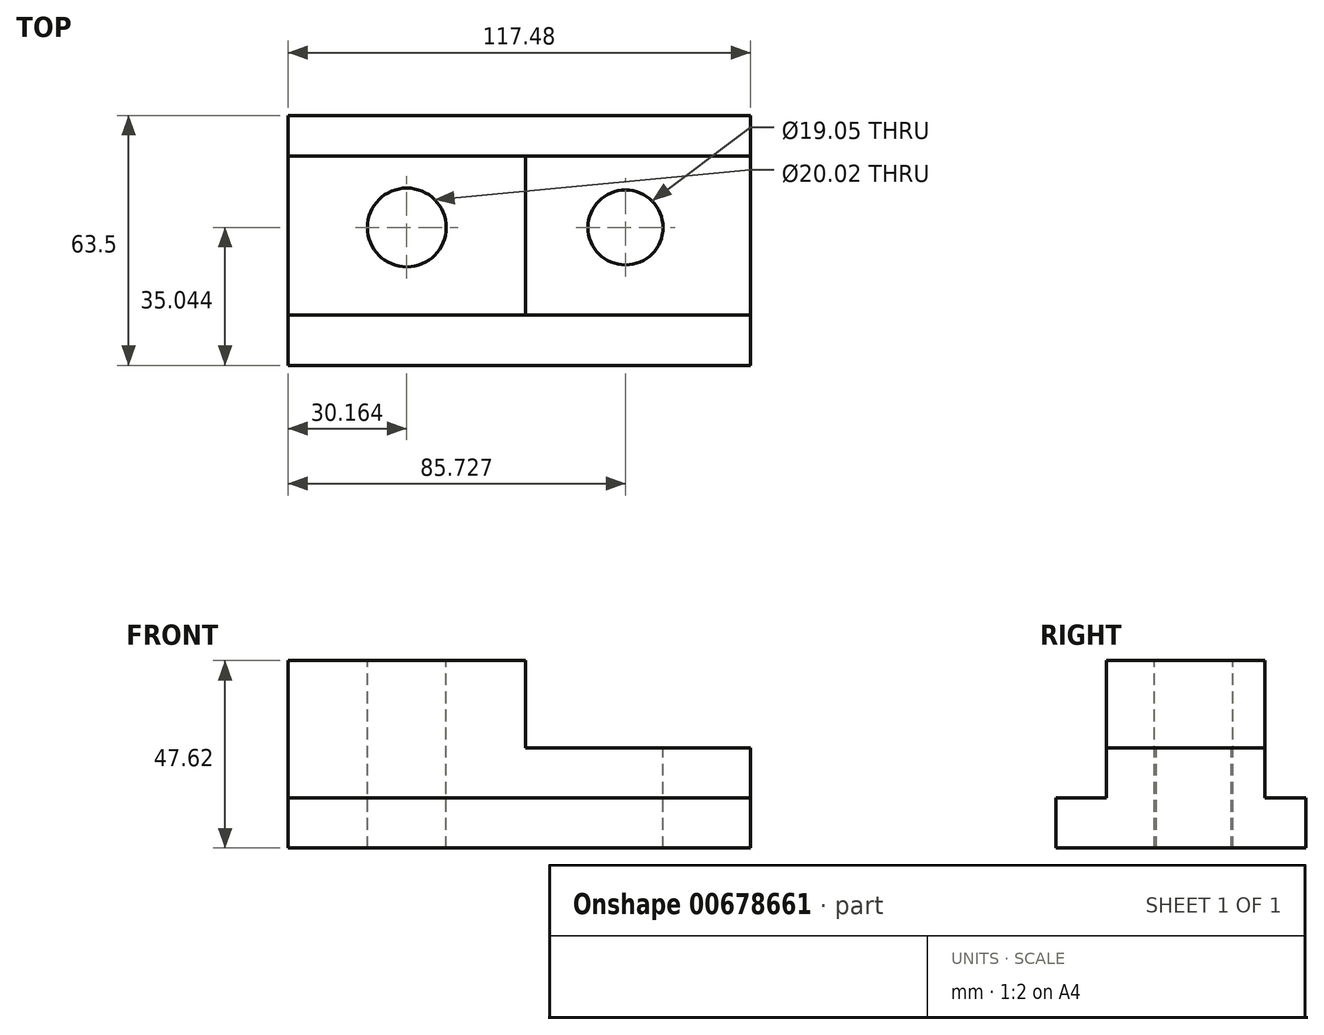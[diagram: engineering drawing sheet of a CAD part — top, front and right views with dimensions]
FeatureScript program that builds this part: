
annotation { "Feature Type Name" : "Feature", "Feature Type Description" : "" }
export const myFeature = defineFeature(function(context is Context, id is Id, definition is map)
    precondition{}
    {
        {
            var Q0;
            Q0=qCreatedBy(makeId("Front.planeOp"),FACE);
            var sketch = newSketch(context, id + "F0", { "sketchPlane" : qUnion([Q0])});
            skLineSegment(sketch, "E0", {"start": v(-53.94, -27.1) * mm, "end": v(63.54, -27.1) * mm});
            skLineSegment(sketch, "E1", {"start": v(-53.94, -27.1) * mm, "end": v(-53.94, -14.4) * mm});
            skLineSegment(sketch, "E2", {"start": v(63.54, -27.1) * mm, "end": v(63.54, -14.4) * mm});
            skLineSegment(sketch, "E3", {"start": v(63.54, -14.4) * mm, "end": v(-53.94, -14.4) * mm});
            skSolve(sketch);
        }
        {
            var Q0;
            Q0=makeQuery(id+"F0.imprint","IMPRINT",FACE,{"disambiguationData":[TD([[makeQuery(id+"F0.imprint","IMPRINT",EDGE,{"derivedFrom":sQuery(id+"F0.wireOp",EDGE,"E0")}),1.0]])]});
            extrude(context, id + "F1", {"entities" : qUnion([Q0]), "depth" : 63.5 * mm, "offsetDistance" : 25.4 * mm});
        }
        {
            var Q0;
            Q0=makeQuery(id+"F1.opExtrude","SWEPT_FACE",FACE,{"disambiguationData":[OSD([sQuery(id+"F0.wireOp",EDGE,"E3")])]});
            var sketch = newSketch(context, id + "F2", { "sketchPlane" : qUnion([Q0])});
            skLineSegment(sketch, "E4", {"start": v(-53.94, -50.68) * mm, "end": v(63.54, -50.68) * mm});
            skLineSegment(sketch, "E5", {"start": v(63.54, -50.68) * mm, "end": v(63.54, -10.36) * mm});
            skLineSegment(sketch, "E6", {"start": v(63.54, -10.36) * mm, "end": v(-53.94, -10.36) * mm});
            skLineSegment(sketch, "E7", {"start": v(-53.94, -10.36) * mm, "end": v(-53.94, -50.68) * mm});
            skSolve(sketch);
        }
        {
            var Q0;
            Q0=makeQuery(id+"F2.imprint","IMPRINT",FACE,{"disambiguationData":[TD([[makeQuery(id+"F2.imprint","IMPRINT",EDGE,{"derivedFrom":sQuery(id+"F2.wireOp",EDGE,"E4")}),1.0]])]});
            extrude(context, id + "F3", {"entities" : qUnion([Q0]), "operationType" : NewBodyOperationType.ADD, "depth" : 12.7 * mm, "offsetDistance" : 25.4 * mm});
        }
        {
            var Q0;
            Q0=makeQuery(id+"F3.opExtrude","CAP_FACE",FACE,{"disambiguationData":[OSD([sQuery(id+"F2.wireOp",EDGE,"E4"),sQuery(id+"F2.wireOp",EDGE,"E5"),sQuery(id+"F2.wireOp",EDGE,"E6"),sQuery(id+"F2.wireOp",EDGE,"E7")])],"isStart":false});
            var sketch = newSketch(context, id + "F4", { "sketchPlane" : qUnion([Q0])});
            skLineSegment(sketch, "E8", {"start": v(-53.94, -10.36) * mm, "end": v(-53.94, -50.68) * mm});
            skLineSegment(sketch, "E9", {"start": v(-53.94, -50.68) * mm, "end": v(6.39, -50.68) * mm});
            skLineSegment(sketch, "E10", {"start": v(6.39, -50.68) * mm, "end": v(6.39, -10.36) * mm});
            skLineSegment(sketch, "E11", {"start": v(6.39, -10.36) * mm, "end": v(-53.94, -10.36) * mm});
            skSolve(sketch);
        }
        {
            var Q0;
            Q0=makeQuery(id+"F4.imprint","IMPRINT",FACE,{"disambiguationData":[TD([[makeQuery(id+"F4.imprint","IMPRINT",EDGE,{"derivedFrom":sQuery(id+"F4.wireOp",EDGE,"E8")}),-1.0]])]});
            extrude(context, id + "F5", {"entities" : qUnion([Q0]), "operationType" : NewBodyOperationType.ADD, "depth" : 22.22 * mm, "offsetDistance" : 25.4 * mm});
        }
        {
            var Q0;
            Q0=makeQuery(id+"F3.opExtrude","CAP_FACE",FACE,{"disambiguationData":[OSD([sQuery(id+"F2.wireOp",EDGE,"E4"),sQuery(id+"F2.wireOp",EDGE,"E5"),sQuery(id+"F2.wireOp",EDGE,"E6"),sQuery(id+"F2.wireOp",EDGE,"E7")])],"isStart":false});
            var sketch = newSketch(context, id + "F6", { "sketchPlane" : qUnion([Q0])});
            skCircle(sketch, "E12", {"center": v(31.79, -28.46) * mm, "radius": 9.53 * mm});
            skSolve(sketch);
        }
        {
            var Q0;
            Q0=makeQuery(id+"F6.imprint","IMPRINT",FACE,{"disambiguationData":[TD([[makeQuery(id+"F6.imprint","IMPRINT",EDGE,{"derivedFrom":sQuery(id+"F6.wireOp",EDGE,"E12")}),1.0]])]});
            extrude(context, id + "F7", {"entities" : qUnion([Q0]), "operationType" : NewBodyOperationType.REMOVE, "oppositeDirection" : true, "depth" : 25.4 * mm, "offsetDistance" : 25.4 * mm});
        }
        {
            var Q0;
            Q0=makeQuery(id+"F5.opExtrude","CAP_FACE",FACE,{"disambiguationData":[OSD([sQuery(id+"F4.wireOp",EDGE,"E8"),sQuery(id+"F4.wireOp",EDGE,"E9"),sQuery(id+"F4.wireOp",EDGE,"E10"),sQuery(id+"F4.wireOp",EDGE,"E11")])],"isStart":false});
            var sketch = newSketch(context, id + "F8", { "sketchPlane" : qUnion([Q0])});
            skCircle(sketch, "E13", {"center": v(-23.78, -28.46) * mm, "radius": 10.01 * mm});
            skSolve(sketch);
        }
        {
            var Q0;
            Q0=makeQuery(id+"F8.imprint","IMPRINT",FACE,{"disambiguationData":[TD([[makeQuery(id+"F8.imprint","IMPRINT",EDGE,{"derivedFrom":sQuery(id+"F8.wireOp",EDGE,"E13")}),1.0]])]});
            extrude(context, id + "F9", {"entities" : qUnion([Q0]), "operationType" : NewBodyOperationType.REMOVE, "oppositeDirection" : true, "depth" : 47.88 * mm, "offsetDistance" : 25.4 * mm});
        }
    });
